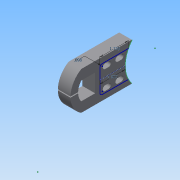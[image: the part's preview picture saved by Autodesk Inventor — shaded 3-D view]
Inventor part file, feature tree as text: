
AUTODESK INVENTOR PART (.ipt)
format: ipt  version: 2015 (Build 190159000, 159)  size: 136,704 bytes
history: native  units: in
note: dims shown in document units (in); Inventor stores cm internally (conversion verified against a paired STEP export)
features: sketch x2, extrude x1
ambient origin geometry x8: Origin, YZ Plane, XZ Plane, XY Plane, X Axis, Y Axis, Z Axis, Center Point
bodies: Solid1 (feature_tree)
feature tree (3):
  extrude  "Extrusion1"  Depth=0.71in
  sketch  "Sketch2"  dims[d2=0.1in d4=1.1811in d8=0.196in d9=0.098in d17=0.125in d18=0.7874in d20=0.5in d21=0.7874in d23=0.75in d26=1.5in d30=0.4in d31=0.3in d32=2.6394in d33=0.0394in d34=0.5in d35=0.0in d37=1.0in d38=1.125in d39=0.098in]
  sketch  "Sketch1"  dims[d0=0.55in d1=0.71in]
